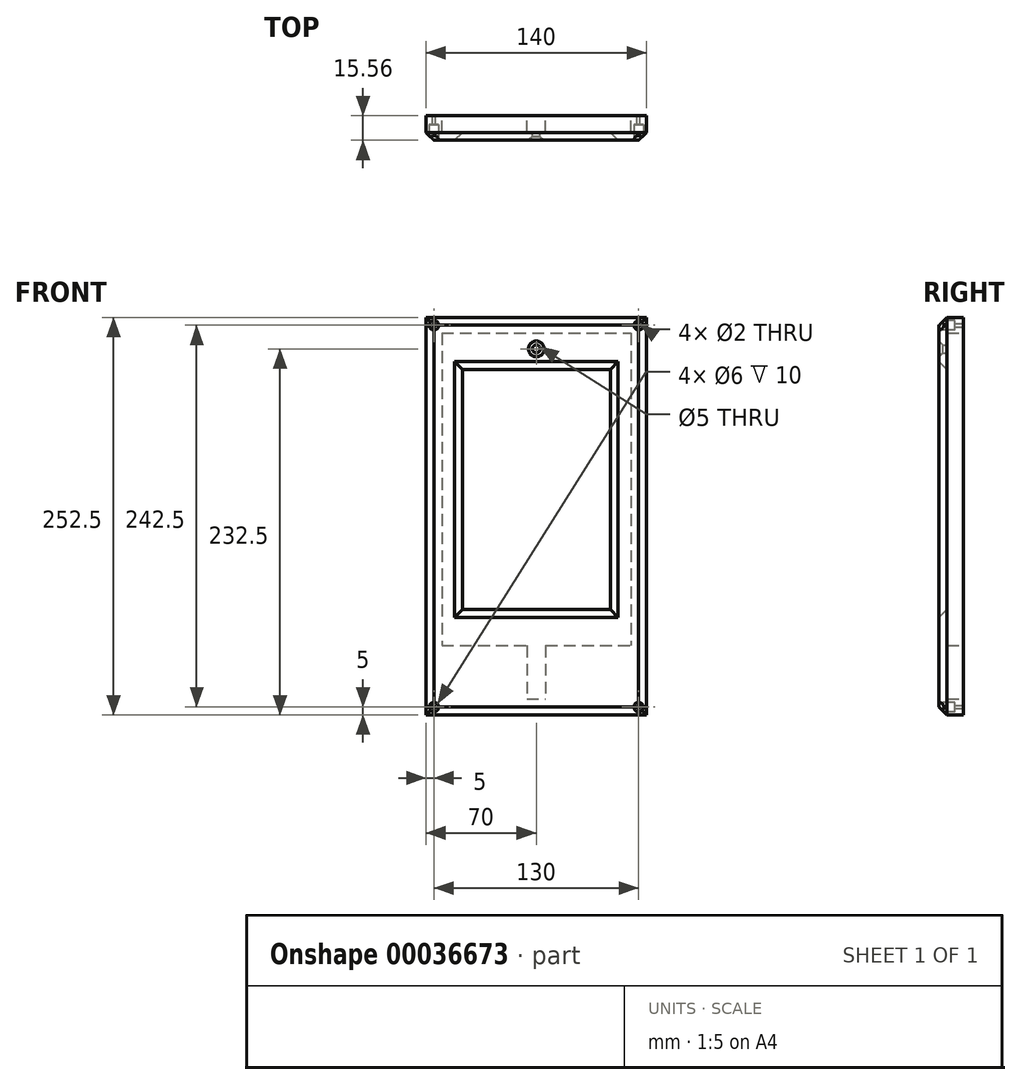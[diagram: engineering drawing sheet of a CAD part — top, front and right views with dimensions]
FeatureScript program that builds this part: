
annotation { "Feature Type Name" : "Feature", "Feature Type Description" : "" }
export const myFeature = defineFeature(function(context is Context, id is Id, definition is map)
    precondition{}
    {
        {
            var Q0;
            Q0=qCreatedBy(makeId("Front.planeOp"),FACE);
            var sketch = newSketch(context, id + "F0", { "sketchPlane" : qUnion([Q0])});
            skLineSegment(sketch, "E0.bottom", {"start": v(0, 0) * mm, "end": v(-140, 0) * mm});
            skLineSegment(sketch, "E0.top", {"start": v(0, 252.5) * mm, "end": v(-140, 252.5) * mm});
            skLineSegment(sketch, "E0.left", {"start": v(0, 0) * mm, "end": v(0, 252.5) * mm});
            skLineSegment(sketch, "E0.right", {"start": v(-140, 0) * mm, "end": v(-140, 252.5) * mm});
            skLineSegment(sketch, "E1.bottom", {"start": v(-130, 242.5) * mm, "end": v(-10, 242.5) * mm});
            skLineSegment(sketch, "E1.top", {"start": v(-130, 44) * mm, "end": v(-10, 44) * mm});
            skLineSegment(sketch, "E1.left", {"start": v(-130, 242.5) * mm, "end": v(-130, 44) * mm});
            skLineSegment(sketch, "E1.right", {"start": v(-10, 242.5) * mm, "end": v(-10, 44) * mm});
            skLineSegment(sketch, "E2.bottom", {"start": v(-117, 219.5) * mm, "end": v(-23, 219.5) * mm});
            skLineSegment(sketch, "E2.top", {"start": v(-117, 67) * mm, "end": v(-23, 67) * mm});
            skLineSegment(sketch, "E2.left", {"start": v(-117, 219.5) * mm, "end": v(-117, 67) * mm});
            skLineSegment(sketch, "E2.right", {"start": v(-23, 219.5) * mm, "end": v(-23, 67) * mm});
            skLineSegment(sketch, "E3.bottom", {"start": v(-76, 44) * mm, "end": v(-64, 44) * mm});
            skLineSegment(sketch, "E3.top", {"start": v(-76, 10) * mm, "end": v(-64, 10) * mm});
            skLineSegment(sketch, "E3.left", {"start": v(-76, 44) * mm, "end": v(-76, 10) * mm});
            skLineSegment(sketch, "E3.right", {"start": v(-64, 44) * mm, "end": v(-64, 10) * mm});
            skCircle(sketch, "E4", {"center": v(-70, 232.5) * mm, "radius": 2.5 * mm});
            skCircle(sketch, "E5", {"center": v(-135, 247.5) * mm, "radius": 1 * mm});
            skLineSegment(sketch, "E6.direction1", {"start": v(-135, 247.5) * mm, "end": v(-5, 247.5) * mm, "construction": true});
            skLineSegment(sketch, "E6.direction2", {"start": v(-135, 247.5) * mm, "end": v(-135, 5) * mm, "construction": true});
            skCircle(sketch, "E7.0.1.0", {"center": v(-135, 5) * mm, "radius": 1 * mm});
            skCircle(sketch, "E7.1.0.0", {"center": v(-5, 247.5) * mm, "radius": 1 * mm});
            skCircle(sketch, "E7.1.1.0", {"center": v(-5, 5) * mm, "radius": 1 * mm});
            skSolve(sketch);
        }
        {
            var Q0;
            Q0=makeQuery(id+"F0.imprint","IMPRINT",FACE,{"disambiguationData":[TD([[makeQuery(id+"F0.imprint","IMPRINT",EDGE,{"derivedFrom":sQuery(id+"F0.wireOp",EDGE,"E0.bottom")}),-1.0]])]});
            var Q1;
            Q1=makeQuery(id+"F0.imprint","IMPRINT",FACE,{"disambiguationData":[TD([[makeQuery(id+"F0.imprint","IMPRINT",EDGE,{"derivedFrom":sQuery(id+"F0.wireOp",EDGE,"E3.top")}),1.0]])]});
            var Q2;
            Q2=makeQuery(id+"F0.imprint","IMPRINT",FACE,{"disambiguationData":[TD([[makeQuery(id+"F0.imprint","IMPRINT",EDGE,{"derivedFrom":sQuery(id+"F0.wireOp",EDGE,"E1.bottom")}),-1.0]])]});
            var Q3;
            Q3=makeQuery(id+"F0.imprint","IMPRINT",FACE,{"disambiguationData":[TD([[makeQuery(id+"F0.imprint","IMPRINT",EDGE,{"derivedFrom":sQuery(id+"F0.wireOp",EDGE,"E6.1.1.0")}),1.0]])]});
            var Q4;
            Q4=makeQuery(id+"F0.imprint","IMPRINT",FACE,{"disambiguationData":[TD([[makeQuery(id+"F0.imprint","IMPRINT",EDGE,{"derivedFrom":sQuery(id+"F0.wireOp",EDGE,"E6.0.1.0")}),1.0]])]});
            var Q5;
            Q5=makeQuery(id+"F0.imprint","IMPRINT",FACE,{"disambiguationData":[TD([[makeQuery(id+"F0.imprint","IMPRINT",EDGE,{"derivedFrom":sQuery(id+"F0.wireOp",EDGE,"E6.1.0.0")}),1.0]])]});
            var Q6;
            Q6=makeQuery(id+"F0.imprint","IMPRINT",FACE,{"disambiguationData":[TD([[makeQuery(id+"F0.imprint","IMPRINT",EDGE,{"derivedFrom":sQuery(id+"F0.wireOp",EDGE,"E0.bottom")}),-1.0]])]});
            extrude(context, id + "F1", {"entities" : qUnion([Q0, Q1, Q2, Q3, Q4, Q5, Q6]), "depth" : (10.56 + 5) * mm});
        }
        {
            var Q0;
            Q0=makeQuery(id+"F0.imprint","IMPRINT",FACE,{"disambiguationData":[TD([[makeQuery(id+"F0.imprint","IMPRINT",EDGE,{"derivedFrom":sQuery(id+"F0.wireOp",EDGE,"E1.bottom")}),-1.0]])]});
            var Q1;
            Q1=makeQuery(id+"F0.imprint","IMPRINT",FACE,{"disambiguationData":[TD([[makeQuery(id+"F0.imprint","IMPRINT",EDGE,{"derivedFrom":sQuery(id+"F0.wireOp",EDGE,"E3.top")}),1.0]])]});
            extrude(context, id + "F2", {"entities" : qUnion([Q0, Q1]), "operationType" : NewBodyOperationType.REMOVE, "depth" : 10.56 * mm});
        }
        {
            var Q0;
            Q0=makeQuery(id+"F1.opExtrude","CAP_EDGE",EDGE,{"disambiguationData":[OSD([sQuery(id+"F0.wireOp",EDGE,"E0.bottom")])],"isStart":false});
            var Q1;
            Q1=makeQuery(id+"F1.opExtrude","CAP_EDGE",EDGE,{"disambiguationData":[OSD([sQuery(id+"F0.wireOp",EDGE,"E0.right")])],"isStart":false});
            var Q2;
            Q2=makeQuery(id+"F1.opExtrude","CAP_EDGE",EDGE,{"disambiguationData":[OSD([sQuery(id+"F0.wireOp",EDGE,"E0.left")])],"isStart":false});
            var Q3;
            Q3=makeQuery(id+"F1.opExtrude","CAP_EDGE",EDGE,{"disambiguationData":[OSD([sQuery(id+"F0.wireOp",EDGE,"E0.top")])],"isStart":false});
            chamfer(context, id + "F3", {"entities" : qUnion([Q0, Q1, Q2, Q3]), "width" : 5 * mm, "tangentPropagation" : true});
        }
        {
            var Q0;
            Q0=makeQuery(id+"F1.opExtrude","CAP_EDGE",EDGE,{"disambiguationData":[OSD([sQuery(id+"F0.wireOp",EDGE,"E4")])],"isStart":false});
            chamfer(context, id + "F4", {"entities" : qUnion([Q0]), "width" : 2.5 * mm, "tangentPropagation" : true});
        }
        {
            var Q0;
            Q0=makeQuery(id+"F1.opExtrude","CAP_FACE",FACE,{"disambiguationData":[OSD([sQuery(id+"F0.wireOp",EDGE,"E0.bottom"),sQuery(id+"F0.wireOp",EDGE,"E0.top"),sQuery(id+"F0.wireOp",EDGE,"E0.left"),sQuery(id+"F0.wireOp",EDGE,"E0.right"),sQuery(id+"F0.wireOp",EDGE,"E2.bottom"),sQuery(id+"F0.wireOp",EDGE,"E2.top"),sQuery(id+"F0.wireOp",EDGE,"E2.left"),sQuery(id+"F0.wireOp",EDGE,"E2.right"),sQuery(id+"F0.wireOp",EDGE,"E4"),sQuery(id+"F0.wireOp",EDGE,"E5"),sQuery(id+"F0.wireOp",EDGE,"E7.0.1.0"),sQuery(id+"F0.wireOp",EDGE,"E7.1.0.0"),sQuery(id+"F0.wireOp",EDGE,"E7.1.1.0")])],"isStart":false});
            var sketch = newSketch(context, id + "F5", { "sketchPlane" : qUnion([Q0])});
            skCircle(sketch, "E8", {"center": v(-135, 247.5) * mm, "radius": 3 * mm});
            skCircle(sketch, "E9.0.1.0", {"center": v(-135, 5) * mm, "radius": 3 * mm});
            skCircle(sketch, "E9.1.0.0", {"center": v(-5, 247.5) * mm, "radius": 3 * mm});
            skCircle(sketch, "E9.1.1.0", {"center": v(-5, 5) * mm, "radius": 3 * mm});
            skLineSegment(sketch, "E9.direction1", {"start": v(-135, 247.5) * mm, "end": v(-5, 247.5) * mm, "construction": true});
            skLineSegment(sketch, "E9.direction2", {"start": v(-135, 247.5) * mm, "end": v(-135, 5) * mm, "construction": true});
            skSolve(sketch);
        }
        {
            var Q0;
            Q0 = qSketchRegion(id + "F5", true);
            extrude(context, id + "F6", {"entities" : qUnion([Q0]), "operationType" : NewBodyOperationType.REMOVE, "oppositeDirection" : true, "depth" : 10 * mm});
        }
        {
            var Q0;
            Q0=makeQuery(id+"F1.opExtrude","CAP_EDGE",EDGE,{"disambiguationData":[OSD([sQuery(id+"F0.wireOp",EDGE,"E2.top")])],"isStart":false});
            var Q1;
            Q1=makeQuery(id+"F1.opExtrude","CAP_EDGE",EDGE,{"disambiguationData":[OSD([sQuery(id+"F0.wireOp",EDGE,"E2.left")])],"isStart":false});
            var Q2;
            Q2=makeQuery(id+"F1.opExtrude","CAP_EDGE",EDGE,{"disambiguationData":[OSD([sQuery(id+"F0.wireOp",EDGE,"E2.right")])],"isStart":false});
            var Q3;
            Q3=makeQuery(id+"F1.opExtrude","CAP_EDGE",EDGE,{"disambiguationData":[OSD([sQuery(id+"F0.wireOp",EDGE,"E2.bottom")])],"isStart":false});
            chamfer(context, id + "F7", {"entities" : qUnion([Q0, Q1, Q2, Q3]), "width" : 5 * mm, "tangentPropagation" : true});
        }
    });
